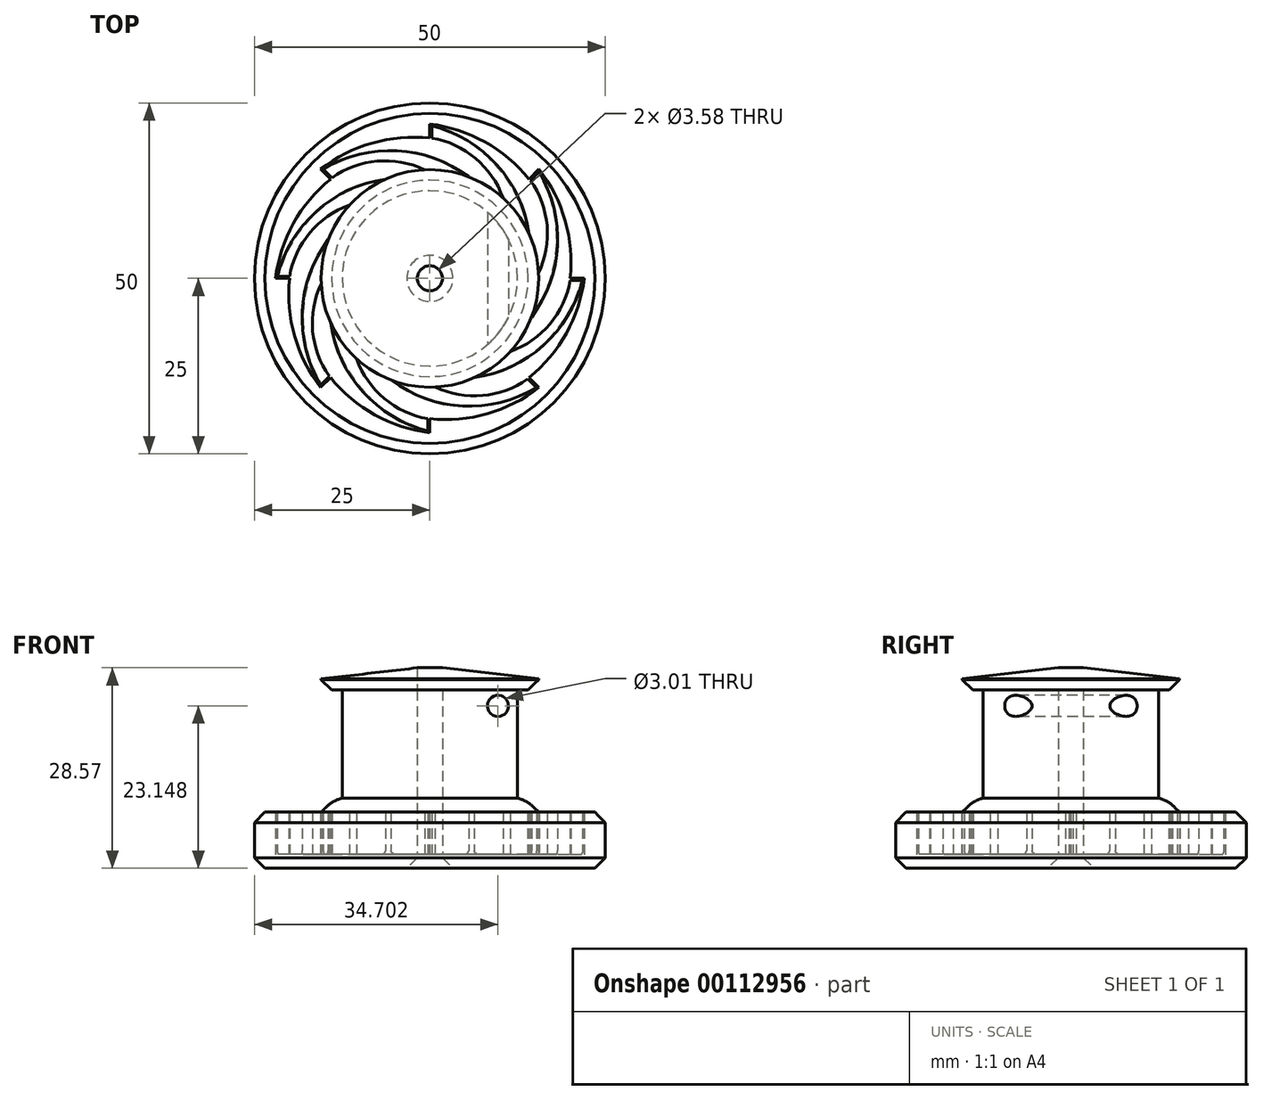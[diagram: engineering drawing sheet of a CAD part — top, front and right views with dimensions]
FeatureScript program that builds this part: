
annotation { "Feature Type Name" : "Feature", "Feature Type Description" : "" }
export const myFeature = defineFeature(function(context is Context, id is Id, definition is map)
    precondition{}
    {
        {
            var Q0;
            Q0=qCreatedBy(makeId("Top.planeOp"),FACE);
            var sketch = newSketch(context, id + "F0", { "sketchPlane" : qUnion([Q0])});
            skCircle(sketch, "E0", {"center": v(0, 0) * mm, "radius": 25 * mm});
            skCircle(sketch, "E1", {"center": v(0, 0) * mm, "radius": 1.8 * mm});
            skArc(sketch, "E2", {"start": v(-0.75, 15.48) * mm, "mid": v(-3.6, 15.08) * mm, "end": v(-6.33, 14.15) * mm});
            skLineSegment(sketch, "E3", {"start": v(0, 25) * mm, "end": v(0, -25) * mm, "construction": true});
            skLineSegment(sketch, "E4", {"start": v(-25, 0) * mm, "end": v(25, 0) * mm, "construction": true});
            skLineSegment(sketch, "E5", {"start": v(-17.68, 17.68) * mm, "end": v(17.68, -17.68) * mm, "construction": true});
            skLineSegment(sketch, "E6", {"start": v(17.68, 17.68) * mm, "end": v(-17.68, -17.68) * mm, "construction": true});
            skArc(sketch, "E7", {"start": v(0, 20) * mm, "mid": v(-8.2, 19.29) * mm, "end": v(-15.56, 15.56) * mm});
            skLineSegment(sketch, "E8", {"start": v(0, 22) * mm, "end": v(0, 20) * mm});
            skLineSegment(sketch, "E9", {"start": v(0.28, 20) * mm, "end": v(0.28, 21.75) * mm});
            skArc(sketch, "E10.1.0", {"start": v(-14.14, 14.14) * mm, "mid": v(-19.44, 7.83) * mm, "end": v(-22, 0) * mm});
            skLineSegment(sketch, "E10.1.1", {"start": v(-15.56, 15.56) * mm, "end": v(-14.14, 14.14) * mm});
            skArc(sketch, "E10.2.0", {"start": v(-20, 0) * mm, "mid": v(-19.29, -8.2) * mm, "end": v(-15.56, -15.56) * mm});
            skLineSegment(sketch, "E10.2.1", {"start": v(-22, 0) * mm, "end": v(-20, 0) * mm});
            skArc(sketch, "E10.3.0", {"start": v(-14.14, -14.14) * mm, "mid": v(-7.83, -19.44) * mm, "end": v(0, -22) * mm});
            skLineSegment(sketch, "E10.3.1", {"start": v(-15.56, -15.56) * mm, "end": v(-14.14, -14.14) * mm});
            skArc(sketch, "E10.4.0", {"start": v(0, -20) * mm, "mid": v(8.2, -19.29) * mm, "end": v(15.56, -15.56) * mm});
            skLineSegment(sketch, "E10.4.1", {"start": v(0, -22) * mm, "end": v(0, -20) * mm});
            skArc(sketch, "E10.5.0", {"start": v(14.14, -14.14) * mm, "mid": v(19.44, -7.83) * mm, "end": v(22, 0) * mm});
            skLineSegment(sketch, "E10.5.1", {"start": v(15.56, -15.56) * mm, "end": v(14.14, -14.14) * mm});
            skArc(sketch, "E10.6.0", {"start": v(20, 0) * mm, "mid": v(19.29, 8.2) * mm, "end": v(15.56, 15.56) * mm});
            skLineSegment(sketch, "E10.6.1", {"start": v(22, 0) * mm, "end": v(20, 0) * mm});
            skArc(sketch, "E10.7.0", {"start": v(14.14, 14.14) * mm, "mid": v(7.83, 19.44) * mm, "end": v(0, 22) * mm});
            skLineSegment(sketch, "E10.7.1", {"start": v(15.56, 15.56) * mm, "end": v(14.14, 14.14) * mm});
            skArc(sketch, "E11", {"start": v(14.15, 6.33) * mm, "mid": v(9.57, 16.16) * mm, "end": v(0.28, 21.75) * mm});
            skArc(sketch, "E12", {"start": v(10.42, 11.48) * mm, "mid": v(6.5, 17.12) * mm, "end": v(0.28, 20) * mm});
            skArc(sketch, "E13.1.0", {"start": v(-0.75, 15.48) * mm, "mid": v(-7.5, 16.7) * mm, "end": v(-13.94, 14.34) * mm});
            skArc(sketch, "E13.1.1", {"start": v(5.53, 14.48) * mm, "mid": v(-4.66, 18.2) * mm, "end": v(-15.18, 15.57) * mm});
            skLineSegment(sketch, "E13.1.2", {"start": v(-13.94, 14.34) * mm, "end": v(-15.18, 15.57) * mm});
            skArc(sketch, "E13.2.0", {"start": v(-11.48, 10.42) * mm, "mid": v(-17.12, 6.5) * mm, "end": v(-20, 0.28) * mm});
            skArc(sketch, "E13.2.1", {"start": v(-6.33, 14.15) * mm, "mid": v(-16.16, 9.57) * mm, "end": v(-21.75, 0.28) * mm});
            skLineSegment(sketch, "E13.2.2", {"start": v(-20, 0.28) * mm, "end": v(-21.75, 0.28) * mm});
            skArc(sketch, "E13.3.0", {"start": v(-15.48, -0.75) * mm, "mid": v(-16.7, -7.5) * mm, "end": v(-14.34, -13.94) * mm});
            skArc(sketch, "E13.3.1", {"start": v(-14.48, 5.53) * mm, "mid": v(-18.2, -4.66) * mm, "end": v(-15.57, -15.18) * mm});
            skLineSegment(sketch, "E13.3.2", {"start": v(-14.34, -13.94) * mm, "end": v(-15.57, -15.18) * mm});
            skArc(sketch, "E13.4.0", {"start": v(-10.42, -11.48) * mm, "mid": v(-6.5, -17.12) * mm, "end": v(-0.28, -20) * mm});
            skArc(sketch, "E13.4.1", {"start": v(-14.15, -6.33) * mm, "mid": v(-9.57, -16.16) * mm, "end": v(-0.28, -21.75) * mm});
            skLineSegment(sketch, "E13.4.2", {"start": v(-0.28, -20) * mm, "end": v(-0.28, -21.75) * mm});
            skArc(sketch, "E13.5.0", {"start": v(0.75, -15.48) * mm, "mid": v(7.5, -16.7) * mm, "end": v(13.94, -14.34) * mm});
            skArc(sketch, "E13.5.1", {"start": v(-5.53, -14.48) * mm, "mid": v(4.66, -18.2) * mm, "end": v(15.18, -15.57) * mm});
            skLineSegment(sketch, "E13.5.2", {"start": v(13.94, -14.34) * mm, "end": v(15.18, -15.57) * mm});
            skArc(sketch, "E13.6.0", {"start": v(11.48, -10.42) * mm, "mid": v(17.12, -6.5) * mm, "end": v(20, -0.28) * mm});
            skArc(sketch, "E13.6.1", {"start": v(6.33, -14.15) * mm, "mid": v(16.16, -9.57) * mm, "end": v(21.75, -0.28) * mm});
            skLineSegment(sketch, "E13.6.2", {"start": v(20, -0.28) * mm, "end": v(21.75, -0.28) * mm});
            skArc(sketch, "E13.7.0", {"start": v(15.48, 0.75) * mm, "mid": v(16.7, 7.5) * mm, "end": v(14.34, 13.94) * mm});
            skArc(sketch, "E13.7.1", {"start": v(14.48, -5.53) * mm, "mid": v(18.2, 4.66) * mm, "end": v(15.57, 15.18) * mm});
            skLineSegment(sketch, "E13.7.2", {"start": v(14.34, 13.94) * mm, "end": v(15.57, 15.18) * mm});
            skArc(sketch, "E14.trimOffspring", {"start": v(10.42, 11.48) * mm, "mid": v(8.11, 13.2) * mm, "end": v(5.53, 14.48) * mm});
            skArc(sketch, "E15.trimOffspring", {"start": v(15.48, 0.75) * mm, "mid": v(15.08, 3.6) * mm, "end": v(14.15, 6.33) * mm});
            skArc(sketch, "E16.trimOffspring", {"start": v(11.48, -10.42) * mm, "mid": v(13.2, -8.11) * mm, "end": v(14.48, -5.53) * mm});
            skArc(sketch, "E17.trimOffspring", {"start": v(-11.48, 10.42) * mm, "mid": v(-13.2, 8.11) * mm, "end": v(-14.48, 5.53) * mm});
            skArc(sketch, "E18.trimOffspring", {"start": v(-15.48, -0.75) * mm, "mid": v(-15.08, -3.6) * mm, "end": v(-14.15, -6.33) * mm});
            skArc(sketch, "E19.trimOffspring", {"start": v(-10.42, -11.48) * mm, "mid": v(-8.11, -13.2) * mm, "end": v(-5.53, -14.48) * mm});
            skArc(sketch, "E20.trimOffspring", {"start": v(0.75, -15.48) * mm, "mid": v(3.6, -15.08) * mm, "end": v(6.33, -14.15) * mm});
            skSolve(sketch);
        }
        {
            var Q0;
            Q0=makeQuery(id+"F0.imprint","IMPRINT",FACE,{"disambiguationData":[TD([[makeQuery(id+"F0.imprint","IMPRINT",EDGE,{"derivedFrom":sQuery(id+"F0.wireOp",EDGE,"E0")}),1.0]])]});
            var Q1;
            Q1=makeQuery(id+"F0.imprint","IMPRINT",FACE,{"disambiguationData":[TD([[makeQuery(id+"F0.imprint","IMPRINT",EDGE,{"derivedFrom":sQuery(id+"F0.wireOp",EDGE,"E2")}),-1.0]])]});
            var Q2;
            Q2=makeQuery(id+"F0.imprint","IMPRINT",FACE,{"disambiguationData":[TD([[makeQuery(id+"F0.imprint","IMPRINT",EDGE,{"derivedFrom":sQuery(id+"F0.wireOp",EDGE,"E1")}),-1.0]])]});
            extrude(context, id + "F1", {"entities" : qUnion([Q0, Q1, Q2]), "oppositeDirection" : true, "depth" : 1.5 * mm});
        }
        {
            var Q0;
            Q0=makeQuery(id+"F0.imprint","IMPRINT",FACE,{"disambiguationData":[TD([[makeQuery(id+"F0.imprint","IMPRINT",EDGE,{"derivedFrom":sQuery(id+"F0.wireOp",EDGE,"E0")}),1.0]])]});
            extrude(context, id + "F2", {"entities" : qUnion([Q0]), "operationType" : NewBodyOperationType.ADD, "depth" : 6.5 * mm});
        }
        {
            var Q0;
            Q0=makeQuery(id+"F0.imprint","IMPRINT",FACE,{"disambiguationData":[TD([[makeQuery(id+"F0.imprint","IMPRINT",EDGE,{"derivedFrom":sQuery(id+"F0.wireOp",EDGE,"E1")}),-1.0]])]});
            var sketch = newSketch(context, id + "F3", { "sketchPlane" : qUnion([Q0])});
            skCircle(sketch, "E21.0", {"center": v(0, 0) * mm, "radius": 1.8 * mm});
            skCircle(sketch, "E22", {"center": v(0, 0) * mm, "radius": 5 * mm});
            skSolve(sketch);
        }
        {
            var Q0;
            Q0=qCreatedBy(makeId("Right.planeOp"),FACE);
            var sketch = newSketch(context, id + "F4", { "sketchPlane" : qUnion([Q0])});
            skLineSegment(sketch, "E23", {"start": v(0, 0) * mm, "end": v(0, 0.5) * mm, "construction": true});
            skLineSegment(sketch, "E24.0", {"start": v(-5, 0) * mm, "end": v(5, 0) * mm});
            skLineSegment(sketch, "E25.0", {"start": v(-1.8, 0) * mm, "end": v(1.8, 0) * mm});
            skLineSegment(sketch, "E26", {"start": v(-1.8, 0) * mm, "end": v(-1.8, 0.5) * mm});
            skLineSegment(sketch, "E27", {"start": v(-5, 0) * mm, "end": v(-1.8, 0.5) * mm});
            skSolve(sketch);
        }
        {
            var Q0;
            {var subQ2=sQuery(id+"F4.wireOp",EDGE,"E26");Q0=makeQuery(id+"F4.imprint","IMPRINT",FACE,{"disambiguationData":[TD([[makeQuery(id+"F4.imprint","IMPRINT",EDGE,{"derivedFrom":subQ2}),1.0]])]});}
            var Q1;
            Q1=sQuery(id+"F4.wireOp",EDGE,"E23");
            revolve(context, id + "F5", {"operationType" : NewBodyOperationType.ADD, "entities" : qUnion([Q0]), "axis" : qUnion([Q1]), "revolveType" : RevolveType.FULL});
        }
        {
            var Q0;
            Q0=makeQuery(id+"F0.imprint","IMPRINT",FACE,{"disambiguationData":[TD([[makeQuery(id+"F0.imprint","IMPRINT",EDGE,{"derivedFrom":sQuery(id+"F0.wireOp",EDGE,"E1")}),-1.0]])]});
            extrude(context, id + "F6", {"entities" : qUnion([Q0]), "depth" : 6.5 * mm});
        }
        {
            var Q0;
            Q0=makeQuery(id+"F6.opExtrude","CAP_FACE",FACE,{"disambiguationData":[OSD([sQuery(id+"F0.wireOp",EDGE,"E1"),sQuery(id+"F0.wireOp",EDGE,"E2"),sQuery(id+"F0.wireOp",EDGE,"E9"),sQuery(id+"F0.wireOp",EDGE,"E11"),sQuery(id+"F0.wireOp",EDGE,"E12"),sQuery(id+"F0.wireOp",EDGE,"E13.1.0"),sQuery(id+"F0.wireOp",EDGE,"E13.1.1"),sQuery(id+"F0.wireOp",EDGE,"E13.1.2"),sQuery(id+"F0.wireOp",EDGE,"E13.2.0"),sQuery(id+"F0.wireOp",EDGE,"E13.2.1"),sQuery(id+"F0.wireOp",EDGE,"E13.2.2"),sQuery(id+"F0.wireOp",EDGE,"E13.3.0"),sQuery(id+"F0.wireOp",EDGE,"E13.3.1"),sQuery(id+"F0.wireOp",EDGE,"E13.3.2"),sQuery(id+"F0.wireOp",EDGE,"E13.4.0"),sQuery(id+"F0.wireOp",EDGE,"E13.4.1"),sQuery(id+"F0.wireOp",EDGE,"E13.4.2"),sQuery(id+"F0.wireOp",EDGE,"E13.5.0"),sQuery(id+"F0.wireOp",EDGE,"E13.5.1"),sQuery(id+"F0.wireOp",EDGE,"E13.5.2"),sQuery(id+"F0.wireOp",EDGE,"E13.6.0"),sQuery(id+"F0.wireOp",EDGE,"E13.6.1"),sQuery(id+"F0.wireOp",EDGE,"E13.6.2"),sQuery(id+"F0.wireOp",EDGE,"E13.7.0"),sQuery(id+"F0.wireOp",EDGE,"E13.7.1"),sQuery(id+"F0.wireOp",EDGE,"E13.7.2"),sQuery(id+"F0.wireOp",EDGE,"E14.trimOffspring"),sQuery(id+"F0.wireOp",EDGE,"E15.trimOffspring"),sQuery(id+"F0.wireOp",EDGE,"E16.trimOffspring"),sQuery(id+"F0.wireOp",EDGE,"E17.trimOffspring"),sQuery(id+"F0.wireOp",EDGE,"E18.trimOffspring"),sQuery(id+"F0.wireOp",EDGE,"E19.trimOffspring"),sQuery(id+"F0.wireOp",EDGE,"E20.trimOffspring")])],"isStart":false});
            var sketch = newSketch(context, id + "F7", { "sketchPlane" : qUnion([Q0])});
            skCircle(sketch, "E28.0", {"center": v(0, 0) * mm, "radius": 1.8 * mm});
            skCircle(sketch, "E29", {"center": v(0, 0) * mm, "radius": 15.5 * mm});
            skCircle(sketch, "E30", {"center": v(0, 0) * mm, "radius": 12.5 * mm});
            skSolve(sketch);
        }
        {
            var Q0;
            Q0=makeQuery(id+"F7.imprint","IMPRINT",FACE,{"disambiguationData":[TD([[makeQuery(id+"F7.imprint","IMPRINT",EDGE,{"derivedFrom":sQuery(id+"F7.wireOp",EDGE,"E28.0")}),-1.0]])]});
            extrude(context, id + "F8", {"entities" : qUnion([Q0]), "operationType" : NewBodyOperationType.ADD, "depth" : 17.4 * mm});
        }
        {
            var Q0;
            Q0=makeQuery(id+"F7.imprint","IMPRINT",FACE,{"disambiguationData":[TD([[makeQuery(id+"F7.imprint","IMPRINT",EDGE,{"derivedFrom":sQuery(id+"F7.wireOp",EDGE,"E30")}),-1.0]])]});
            extrude(context, id + "F9", {"entities" : qUnion([Q0]), "operationType" : NewBodyOperationType.ADD, "depth" : 2 * mm});
        }
        {
            var Q0;
            Q0=makeQuery(id+"F9.opExtrude","CAP_EDGE",EDGE,{"disambiguationData":[OSD([sQuery(id+"F7.wireOp",EDGE,"E29")])],"isStart":false});
            chamfer(context, id + "F10", {"entities" : qUnion([Q0]), "width" : 2 * mm, "tangentPropagation" : true});
        }
        {
            var Q0;
            {var subQ0=sQuery(id+"F7.wireOp",EDGE,"E29");Q0=makeQuery(id+"F10.opChamfer","BLEND_EDGE",EDGE,{"blendedFrom":[makeQuery(id+"F9.opExtrude","CAP_EDGE",EDGE,{"disambiguationData":[OSD([subQ0])],"isStart":false}),makeQuery(id+"F9.opExtrude","CAP_FACE",FACE,{"disambiguationData":[OSD([subQ0,sQuery(id+"F7.wireOp",EDGE,"E30")])],"isStart":false})],"blendedInto":[makeQuery(id+"F9.opExtrude","CAP_FACE",FACE,{"disambiguationData":[OSD([subQ0,sQuery(id+"F7.wireOp",EDGE,"E30")])],"isStart":false})]});}
            fillet(context, id + "F11", {"entities" : qUnion([Q0]), "radius" : 5 * mm, "tangentPropagation" : true, "allowEdgeOverflow" : false});
        }
        {
            var Q0;
            Q0=makeQuery(id+"F8.opExtrude","CAP_FACE",FACE,{"disambiguationData":[OSD([sQuery(id+"F7.wireOp",EDGE,"E28.0"),sQuery(id+"F7.wireOp",EDGE,"E30")])],"isStart":false});
            var sketch = newSketch(context, id + "F12", { "sketchPlane" : qUnion([Q0])});
            skCircle(sketch, "E31.0", {"center": v(0, 0) * mm, "radius": 15.5 * mm});
            skCircle(sketch, "E32.0", {"center": v(0, 0) * mm, "radius": 1.8 * mm});
            skSolve(sketch);
        }
        {
            var Q0;
            Q0=makeQuery(id+"F12.imprint","IMPRINT",FACE,{"disambiguationData":[TD([[makeQuery(id+"F12.imprint","IMPRINT",EDGE,{"derivedFrom":sQuery(id+"F12.wireOp",EDGE,"E31.0")}),1.0]])]});
            var Q1;
            Q1=makeQuery(id+"F12.imprint","IMPRINT",FACE,{"disambiguationData":[TD([[makeQuery(id+"F12.imprint","IMPRINT",EDGE,{"derivedFrom":sQuery(id+"F12.wireOp",EDGE,"E32.0")}),-1.0]])]});
            extrude(context, id + "F13", {"entities" : qUnion([Q0, Q1]), "depth" : 1.59 * mm});
        }
        {
            var Q0;
            Q0=qCreatedBy(makeId("Front.planeOp"),FACE);
            var sketch = newSketch(context, id + "F14", { "sketchPlane" : qUnion([Q0])});
            skLineSegment(sketch, "E33.0", {"start": v(-1.8, 25.49) * mm, "end": v(1.8, 25.49) * mm});
            skLineSegment(sketch, "E34", {"start": v(1.8, 25.49) * mm, "end": v(1.8, 27.07) * mm});
            skLineSegment(sketch, "E35.0", {"start": v(-15.5, 25.49) * mm, "end": v(15.5, 25.49) * mm});
            skLineSegment(sketch, "E36", {"start": v(15.5, 25.49) * mm, "end": v(1.8, 27.07) * mm});
            skLineSegment(sketch, "E37", {"start": v(0, 25.49) * mm, "end": v(0, 28.38) * mm, "construction": true});
            skPoint(sketch, "E37.endSnap0", {"position": v(0, 25.49) * mm});
            skSolve(sketch);
        }
        {
            var Q0;
            {var subQ0=sQuery(id+"F14.wireOp",EDGE,"E34");Q0=makeQuery(id+"F14.imprint","IMPRINT",FACE,{"disambiguationData":[TD([[makeQuery(id+"F14.imprint","IMPRINT",EDGE,{"derivedFrom":subQ0}),-1.0]])]});}
            var Q1;
            Q1=sQuery(id+"F14.wireOp",EDGE,"E37");
            revolve(context, id + "F15", {"operationType" : NewBodyOperationType.ADD, "entities" : qUnion([Q0]), "axis" : qUnion([Q1]), "revolveType" : RevolveType.FULL});
        }
        {
            var Q0;
            Q0=makeQuery(id+"F13.opExtrude","CAP_EDGE",EDGE,{"disambiguationData":[OSD([sQuery(id+"F12.wireOp",EDGE,"E31.0")])],"isStart":true});
            var Q1;
            Q1=makeQuery(id+"F2.opExtrude","CAP_EDGE",EDGE,{"disambiguationData":[OSD([sQuery(id+"F0.wireOp",EDGE,"E0")])],"isStart":false});
            var Q2;
            Q2=makeQuery(id+"F1.opExtrude","CAP_FACE",FACE,{"disambiguationData":[OSD([sQuery(id+"F0.wireOp",EDGE,"E0"),sQuery(id+"F0.wireOp",EDGE,"E1")])],"isStart":false});
            chamfer(context, id + "F16", {"entities" : qUnion([Q0, Q1, Q2]), "width" : 1.5 * mm, "tangentPropagation" : true});
        }
        {
            var Q0;
            Q0=makeQuery(id+"F1.opExtrude","CAP_EDGE",EDGE,{"disambiguationData":[OSD([sQuery(id+"F0.wireOp",EDGE,"E0")])],"isStart":false});
            var Q1;
            Q1=makeQuery(id+"F2.opExtrude","CAP_EDGE",EDGE,{"disambiguationData":[OSD([sQuery(id+"F0.wireOp",EDGE,"E0")])],"isStart":false});
            var Q2;
            Q2=makeQuery(id+"F6.opExtrude","CAP_EDGE",EDGE,{"disambiguationData":[OSD([sQuery(id+"F0.wireOp",EDGE,"E13.4.1")])],"isStart":true});
            var Q3;
            Q3=makeQuery(id+"F6.opExtrude","CAP_EDGE",EDGE,{"disambiguationData":[OSD([sQuery(id+"F0.wireOp",EDGE,"E13.3.1")])],"isStart":true});
            var Q4;
            Q4=makeQuery(id+"F6.opExtrude","CAP_EDGE",EDGE,{"disambiguationData":[OSD([sQuery(id+"F0.wireOp",EDGE,"E13.2.1")])],"isStart":true});
            var Q5;
            Q5=makeQuery(id+"F6.opExtrude","CAP_EDGE",EDGE,{"disambiguationData":[OSD([sQuery(id+"F0.wireOp",EDGE,"E13.1.1")])],"isStart":true});
            var Q6;
            Q6=makeQuery(id+"F6.opExtrude","CAP_EDGE",EDGE,{"disambiguationData":[OSD([sQuery(id+"F0.wireOp",EDGE,"E11")])],"isStart":true});
            var Q7;
            Q7=makeQuery(id+"F6.opExtrude","CAP_EDGE",EDGE,{"disambiguationData":[OSD([sQuery(id+"F0.wireOp",EDGE,"E13.7.1")])],"isStart":true});
            var Q8;
            Q8=makeQuery(id+"F6.opExtrude","CAP_EDGE",EDGE,{"disambiguationData":[OSD([sQuery(id+"F0.wireOp",EDGE,"E13.6.1")])],"isStart":true});
            var Q9;
            Q9=makeQuery(id+"F6.opExtrude","CAP_EDGE",EDGE,{"disambiguationData":[OSD([sQuery(id+"F0.wireOp",EDGE,"E13.5.1")])],"isStart":true});
            fillet(context, id + "F17", {"entities" : qUnion([Q0, Q1, Q2, Q3, Q4, Q5, Q6, Q7, Q8, Q9]), "radius" : 1 * mm, "tangentPropagation" : true, "allowEdgeOverflow" : false});
        }
        {
            var Q0;
            Q0=makeQuery(id+"F0.imprint","IMPRINT",FACE,{"disambiguationData":[TD([[makeQuery(id+"F0.imprint","IMPRINT",EDGE,{"derivedFrom":sQuery(id+"F0.wireOp",EDGE,"E1")}),-1.0]])]});
            extrude(context, id + "F18", {"entities" : qUnion([Q0]), "operationType" : NewBodyOperationType.REMOVE, "depth" : .5 * mm});
        }
        {
            var Q0;
            Q0=qCreatedBy(makeId("Front.planeOp"),FACE);
            var sketch = newSketch(context, id + "F19", { "sketchPlane" : qUnion([Q0])});
            skLineSegment(sketch, "E38", {"start": v(0, 0) * mm, "end": v(0, 21.65) * mm, "construction": true});
            skLineSegment(sketch, "E39", {"start": v(0, 21.65) * mm, "end": v(9.7, 21.65) * mm, "construction": true});
            skCircle(sketch, "E40", {"center": v(9.7, 21.65) * mm, "radius": 1.5 * mm});
            skSolve(sketch);
        }
        {
            var Q0;
            Q0=qSketchRegion(id+"F19",true);
            extrude(context, id + "F20", {"entities" : qUnion([Q0]), "operationType" : NewBodyOperationType.REMOVE, "endBound" : BoundingType.SYMMETRIC, "oppositeDirection" : true, "depth" : 25 * mm});
        }
    });
